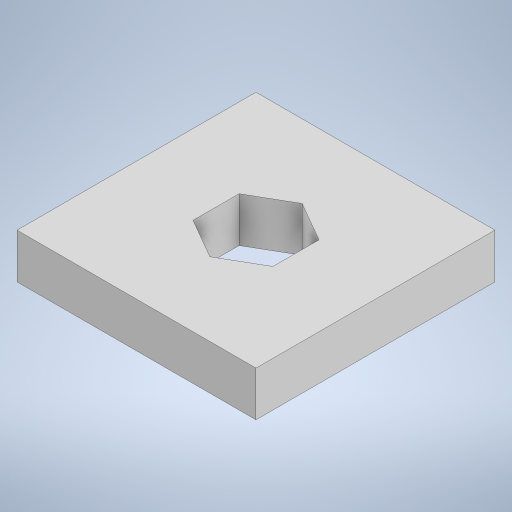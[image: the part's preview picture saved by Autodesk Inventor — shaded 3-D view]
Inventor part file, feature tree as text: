
AUTODESK INVENTOR PART (.ipt)
format: ipt  version: 2023 (Build 270158000, 158)  size: 205,312 bytes
history: native  units: in
note: dims shown in document units (in); Inventor stores cm internally (conversion verified against a paired STEP export)
features: extrude x1, sketch x1
ambient origin geometry x8: Origin, YZ Plane, XZ Plane, XY Plane, X Axis, Y Axis, Z Axis, Center Point
bodies: Solid1 (feature_tree)
feature tree (2):
  extrude  "Extrusion1"  Depth=2.0in
  sketch  "Sketch1"  dims[d0=2.0in d1=2.0in d2=0.5787in d3=0.375in d4=0.0in]
